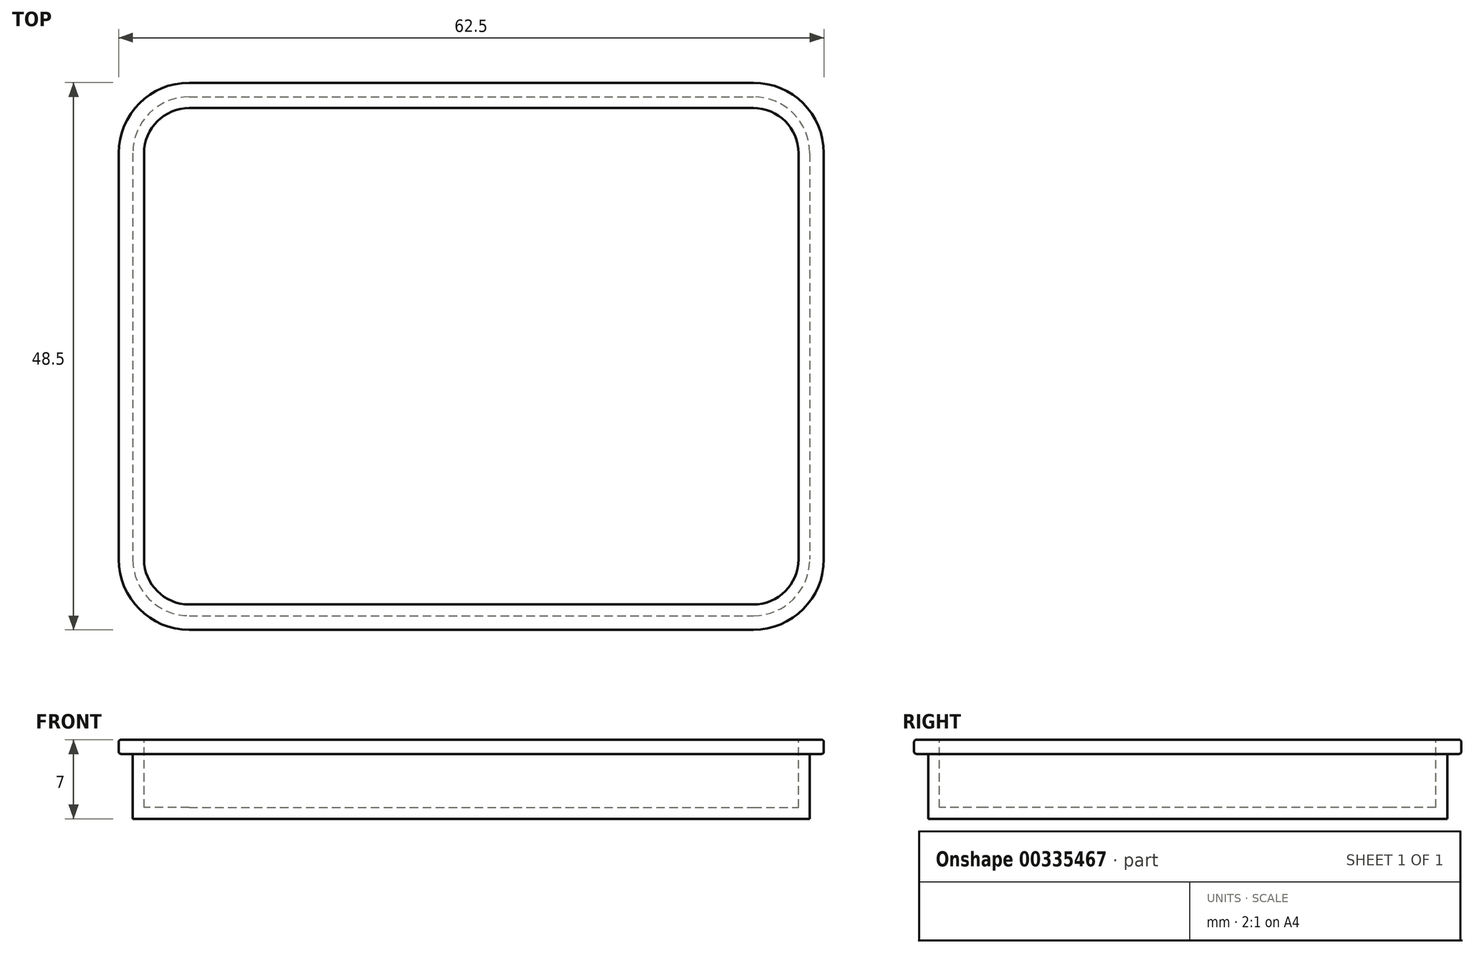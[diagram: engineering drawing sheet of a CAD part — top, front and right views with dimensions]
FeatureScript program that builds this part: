
annotation { "Feature Type Name" : "Feature", "Feature Type Description" : "" }
export const myFeature = defineFeature(function(context is Context, id is Id, definition is map)
    precondition{}
    {
        {
            var Q0;
            Q0=qCreatedBy(makeId("Top.planeOp"),FACE);
            var sketch = newSketch(context, id + "F0", { "sketchPlane" : qUnion([Q0])});
            skLineSegment(sketch, "E0.bottom", {"start": v(-56.01, 8.03) * mm, "end": v(-6.01, 8.03) * mm});
            skLineSegment(sketch, "E0.top", {"start": v(-56.01, -37.97) * mm, "end": v(-6.01, -37.97) * mm});
            skLineSegment(sketch, "E0.left", {"start": v(-61.01, 3.03) * mm, "end": v(-61.01, -32.97) * mm});
            skLineSegment(sketch, "E0.right", {"start": v(-1.01, 3.03) * mm, "end": v(-1.01, -32.97) * mm});
            skPoint(sketch, "E1.visualSharp", {"position": v(-1.01, 8.03) * mm});
            skArc(sketch, "E1.filletArc", {"start": v(-1.01, 3.03) * mm, "mid": v(-2.48, 6.56) * mm, "end": v(-6.01, 8.03) * mm});
            skPoint(sketch, "E2.visualSharp", {"position": v(-1.01, -37.97) * mm});
            skArc(sketch, "E2.filletArc", {"start": v(-6.01, -37.97) * mm, "mid": v(-2.48, -36.5) * mm, "end": v(-1.01, -32.97) * mm});
            skPoint(sketch, "E3.visualSharp", {"position": v(-61.01, 8.03) * mm});
            skArc(sketch, "E3.filletArc", {"start": v(-56.01, 8.03) * mm, "mid": v(-59.55, 6.56) * mm, "end": v(-61.01, 3.03) * mm});
            skPoint(sketch, "E4.visualSharp", {"position": v(-61.01, -37.97) * mm});
            skArc(sketch, "E4.filletArc", {"start": v(-61.01, -32.97) * mm, "mid": v(-59.55, -36.5) * mm, "end": v(-56.01, -37.97) * mm});
            skSolve(sketch);
        }
        {
            var Q0;
            Q0 = qSketchRegion(id + "F0", true);
            extrude(context, id + "F1", {"entities" : qUnion([Q0]), "depth" : 7 * mm});
        }
        {
            var Q0;
            Q0=makeQuery(id+"F1.opExtrude","CAP_FACE",FACE,{"disambiguationData":[OSD([sQuery(id+"F0.wireOp",EDGE,"E0.bottom"),sQuery(id+"F0.wireOp",EDGE,"E0.top"),sQuery(id+"F0.wireOp",EDGE,"E0.left"),sQuery(id+"F0.wireOp",EDGE,"E0.right"),sQuery(id+"F0.wireOp",EDGE,"E1.filletArc"),sQuery(id+"F0.wireOp",EDGE,"E2.filletArc"),sQuery(id+"F0.wireOp",EDGE,"E3.filletArc"),sQuery(id+"F0.wireOp",EDGE,"E4.filletArc")])],"isStart":false});
            var sketch = newSketch(context, id + "F2", { "sketchPlane" : qUnion([Q0])});
            skLineSegment(sketch, "E5.0", {"start": v(-62.26, 3.03) * mm, "end": v(-62.26, -32.97) * mm});
            skArc(sketch, "E5.1", {"start": v(-56.01, 9.28) * mm, "mid": v(-60.43, 7.45) * mm, "end": v(-62.26, 3.03) * mm});
            skArc(sketch, "E5.2", {"start": v(-62.26, -32.97) * mm, "mid": v(-60.43, -37.4) * mm, "end": v(-56.01, -39.22) * mm});
            skLineSegment(sketch, "E5.3", {"start": v(-6.01, 9.28) * mm, "end": v(-56.01, 9.28) * mm});
            skLineSegment(sketch, "E5.4", {"start": v(-56.01, -39.22) * mm, "end": v(-6.01, -39.22) * mm});
            skArc(sketch, "E5.5", {"start": v(-6.01, -39.22) * mm, "mid": v(-1.6, -37.4) * mm, "end": v(0.24, -32.97) * mm});
            skLineSegment(sketch, "E5.6", {"start": v(0.24, -32.97) * mm, "end": v(0.24, 3.03) * mm});
            skArc(sketch, "E5.7", {"start": v(0.24, 3.03) * mm, "mid": v(-1.6, 7.45) * mm, "end": v(-6.01, 9.28) * mm});
            skSolve(sketch);
        }
        {
            var Q0;
            Q0 = qSketchRegion(id + "F2", true);
            extrude(context, id + "F3", {"entities" : qUnion([Q0]), "operationType" : NewBodyOperationType.ADD, "oppositeDirection" : true, "depth" : 1.25 * mm});
        }
        {
            var Q0;
            Q0=makeQuery(id+"F1.opExtrude","CAP_FACE",FACE,{"disambiguationData":[OSD([sQuery(id+"F0.wireOp",EDGE,"E0.bottom"),sQuery(id+"F0.wireOp",EDGE,"E0.top"),sQuery(id+"F0.wireOp",EDGE,"E0.left"),sQuery(id+"F0.wireOp",EDGE,"E0.right"),sQuery(id+"F0.wireOp",EDGE,"E1.filletArc"),sQuery(id+"F0.wireOp",EDGE,"E2.filletArc"),sQuery(id+"F0.wireOp",EDGE,"E3.filletArc"),sQuery(id+"F0.wireOp",EDGE,"E4.filletArc")])],"isStart":false});
            var sketch = newSketch(context, id + "F4", { "sketchPlane" : qUnion([Q0])});
            skLineSegment(sketch, "E6.0", {"start": v(-60.01, 3.03) * mm, "end": v(-60.01, -32.97) * mm});
            skArc(sketch, "E6.1", {"start": v(-56.01, 7.03) * mm, "mid": v(-58.84, 5.86) * mm, "end": v(-60.01, 3.03) * mm});
            skArc(sketch, "E6.2", {"start": v(-60.01, -32.97) * mm, "mid": v(-58.84, -35.8) * mm, "end": v(-56.01, -36.97) * mm});
            skLineSegment(sketch, "E6.3", {"start": v(-6.01, 7.03) * mm, "end": v(-56.01, 7.03) * mm});
            skLineSegment(sketch, "E6.4", {"start": v(-56.01, -36.97) * mm, "end": v(-6.01, -36.97) * mm});
            skArc(sketch, "E6.5", {"start": v(-6.01, -36.97) * mm, "mid": v(-3.18, -35.8) * mm, "end": v(-2.01, -32.97) * mm});
            skLineSegment(sketch, "E6.6", {"start": v(-2.01, -32.97) * mm, "end": v(-2.01, 3.03) * mm});
            skArc(sketch, "E6.7", {"start": v(-2.01, 3.03) * mm, "mid": v(-3.18, 5.86) * mm, "end": v(-6.01, 7.03) * mm});
            skSolve(sketch);
        }
        {
            var Q0;
            Q0 = qSketchRegion(id + "F4", true);
            extrude(context, id + "F5", {"entities" : qUnion([Q0]), "operationType" : NewBodyOperationType.REMOVE, "oppositeDirection" : true, "depth" : 6 * mm, "hasSecondDirection" : true, "secondDirectionOppositeDirection" : false, "secondDirectionDepth" : 25 * mm});
        }
        {
            var Q0;
            Q0=makeQuery(id+"F3.opExtrude","CAP_EDGE",EDGE,{"disambiguationData":[OSD([sQuery(id+"F2.wireOp",EDGE,"E5.0")])],"isStart":true});
            var Q1;
            Q1=makeQuery(id+"F3.opExtrude","CAP_EDGE",EDGE,{"disambiguationData":[OSD([sQuery(id+"F2.wireOp",EDGE,"E5.2")])],"isStart":true});
            var Q2;
            Q2=makeQuery(id+"F3.opExtrude","CAP_EDGE",EDGE,{"disambiguationData":[OSD([sQuery(id+"F2.wireOp",EDGE,"E5.4")])],"isStart":true});
            var Q3;
            Q3=makeQuery(id+"F3.opExtrude","CAP_EDGE",EDGE,{"disambiguationData":[OSD([sQuery(id+"F2.wireOp",EDGE,"E5.5")])],"isStart":true});
            var Q4;
            Q4=makeQuery(id+"F3.opExtrude","CAP_EDGE",EDGE,{"disambiguationData":[OSD([sQuery(id+"F2.wireOp",EDGE,"E5.6")])],"isStart":true});
            var Q5;
            Q5=makeQuery(id+"F3.opExtrude","CAP_EDGE",EDGE,{"disambiguationData":[OSD([sQuery(id+"F2.wireOp",EDGE,"E5.7")])],"isStart":true});
            var Q6;
            Q6=makeQuery(id+"F3.opExtrude","CAP_EDGE",EDGE,{"disambiguationData":[OSD([sQuery(id+"F2.wireOp",EDGE,"E5.3")])],"isStart":true});
            var Q7;
            Q7=makeQuery(id+"F3.opExtrude","CAP_EDGE",EDGE,{"disambiguationData":[OSD([sQuery(id+"F2.wireOp",EDGE,"E5.1")])],"isStart":true});
            var Q8;
            Q8=makeQuery(id+"F3.opExtrude","CAP_EDGE",EDGE,{"disambiguationData":[OSD([sQuery(id+"F2.wireOp",EDGE,"E5.5")])],"isStart":false});
            fillet(context, id + "F6", {"entities" : qUnion([Q0, Q1, Q2, Q3, Q4, Q5, Q6, Q7, Q8]), "radius" : .2 * mm, "tangentPropagation" : true, "allowEdgeOverflow" : false});
        }
    });
